# Revit family: PQHY-P550YLM-A
name_source: partatom
category: Mechanical Equipment
revit_build: Autodesk Revit Architecture 2012 (Build: 20110916_2132(x64)
units: mm (PartAtom-declared; Revit-internal decimal feet)

## types (6) — shared parameters
Compressor Motor Output (kW) = 15
Compressor_Lubricant = MEL32
Compressor_Quantity = 1
Compressor_Type = Inverter scroll hermetic compressor
Cooling Capacity (kW) = 63
Cooling EER (kW/kW) = 5.02
Cooling Power Input (kW) = 12.54
Depth = 550 mm  [stored 1.80446 ft]
Drain pipe1_radius = 13 mm
Drain pipe2_radius = 13 mm
External Finish = Galvanized steel sheets
Gas pipe_radius = 14 mm  [stored 0.0459318 ft]
Heat Source unit Breaker size (A) = 60
Heating COP (kW/kW) = 5.62
Heating Capacity (kW) = 69
Heating Power Input (kW) = 12.27
Height = 1450 mm  [stored 4.75722 ft]
Indoor Unit Model/Quantity = P15 to P250/2 to 47
Indoor Unit Total Capacity = 50 to 130% of heat source unit capacity
Liquid pipe_radius = 8 mm  [stored 0.0262467 ft]
Manufacturer = Mitsubishi Electric Corporation
Maximum Circuit Ampacity (A) = 40.5
Model = PQHY-P550YLM-A
Note_1 = Refrigerant pipe diameters may change depending on the installation condition. Please refer to the installation manual.
Phase = 3
Protection Devices_Compressor = Over-heat protection
Protection Devices_High pressure (MPa) = High pressure sensor, High pressure switch at 4.15
Protection Devices_Inverter circuit (COMP) = Over-heat protection, Over-current protection
Refrigerant Charge (kg) = 11.7
Refrigerant type = R410A
Sound Pressure Level (dB(A)) = 56.5
Space View = Yes
Subcategory = HVAC
URL = http://www.mitsubishielectric.com
Unit Weight (kg) = 246
Water Pipe_radius (Inlet) = 24 mm  [stored 0.0787402 ft]
Water Pipe_radius (Outlet) = 24 mm  [stored 0.0787402 ft]
Water flow rate (m3/h) = 11.52
Width = 880 mm  [stored 2.88714 ft]
zero-valued in all types: Equip_No., SerialNumber, TagNumber

## per-type parameters (varying)
| type | Cooling Current (A) | Cooling Rated Load Ampacity (A) | Heating Current (A) | Heating Rated Load Ampacity (A) | Hertz | Voltage |
| PQHY-P550YLM-A_380V_50Hz | 21.1 | 21.1 | 20.7 | 20.7 | 50 Hz | 380 V |
| PQHY-P550YLM-A_380V_60Hz | 21.1 | 21.1 | 20.7 | 20.7 | 60 Hz | 380 V |
| PQHY-P550YLM-A_400V_50Hz | 20.1 | 20.1 | 19.6 | 19.6 | 50 Hz | 400 V |
| PQHY-P550YLM-A_400V_60Hz | 20.1 | 20.1 | 19.6 | 19.6 | 60 Hz | 400 V |
| PQHY-P550YLM-A_415V_50Hz | 19.3 | 19.3 | 18.9 | 18.9 | 50 Hz | 415 V |
| PQHY-P550YLM-A_415V_60Hz | 19.3 | 19.3 | 18.9 | 18.9 | 60 Hz | 415 V |

note: [stored X ft] marks values corroborated as IEEE doubles in the binary element streams (Revit-internal decimal feet)

## geometry (parser evidence)
native form markers: Blend x6, Sweep x2
no freeform markers — native parametric forms only
